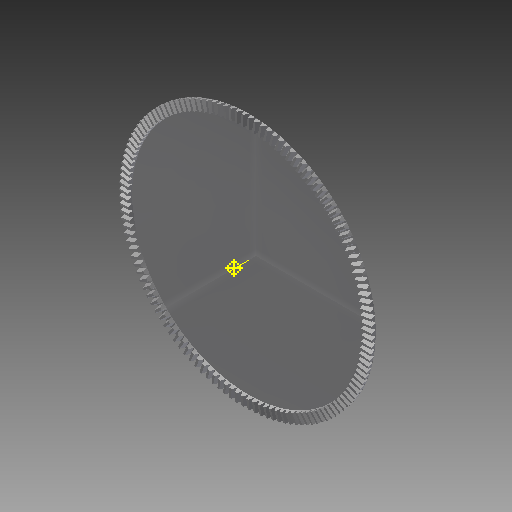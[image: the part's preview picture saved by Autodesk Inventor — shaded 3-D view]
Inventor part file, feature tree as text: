
AUTODESK INVENTOR PART (.ipt)
format: ipt  version: 2017 (Build 210142000, 142)  size: 1,862,656 bytes
history: native  units: mm
features: other x24, loft x2, pattern_circular x2, sketch x1
ambient origin geometry x6: Origin, XZ Plane, X Axis, Y Axis, Z Axis, Center Point
bodies: Solid1 (feature_tree)
feature tree (29):
  other  "Top Point"
  other  "Mesh Plane2"
  other  "Teeth Body"
  other  "Start Point"
  other  "Tooth Plane"
  other  "Start Sketch"
  other  "End Point"
  other  "3D Sketch Right"
  other  "End Plane Right"
  loft  "Loft Right"
  pattern_circular  "Circular Pattern Right"  [2 undecoded]
  other  "3D Sketch Left"
  other  "End Plane Left"
  loft  "Loft Left"
  pattern_circular  "Circular Pattern Left"  [2 undecoded]
  other  "Fix Body"
  other  "Mesh Plane"
  other  "Top Plane"
  other  "Teeth Body Sketch"
  other  "End Plane"
  other  "End Sketch"
  other  "Helical Curve Left"
  other  "End Sketch Left"
  other  "Body Sketch"
  sketch  "Sketch6"  dims[d0=330.2mm d1=329.501251mm d2=330.78229mm d3=12.7mm d4=16.526741mm d5=90.0deg d7=493.522657mm d8=468.312989mm d9=1278.766519mm d11=12.9794mm d12=455.473429mm d15=432.207357mm d16=1180.177168mm d17=0.0mm d18=90.0deg d19=0.0mm d20=90.0deg d21=1300.0mm d22=360.0deg d26=314.208686mm d27=1.487752mm d28=330.2mm d29=-14.559197mm d30=455.473429mm d31=432.207357mm d32=1180.177168mm d35=0.0mm d37=0.0mm d39=0.0mm d40=90.0deg d41=1300.0mm d42=360.0deg d46=90.0deg d47=90.0deg d48=0.0mm d49=0.0mm d50=90.0deg d51=0.241661mm d52=0.0mm d53=0.0mm d54=0.0mm d56=17.557566mm d57=1444.576572mm d58=1436.641612mm d59=1333.203726mm d60=1325.880529mm d61=1333.203726mm d62=1325.880529mm d63=90.0deg d64=90.0deg d65=314.208686mm d66=31.5mm d67=330.2mm d68=-14.559197mm d69=1.487752mm d70=432.207357mm d71=1180.177168mm d72=455.473429mm d73=1325.880529mm d74=1333.203726mm d75=0.0mm d76=90.0deg d77=0.0mm d78=90.0deg d79=0.0mm d80=90.0deg d81=1300.0mm d82=360.0deg d84=10.0mm d85=20.0mm d86=20.0mm d87=10.0mm d88=0.0mm d89=0.0mm]
  other  "Srf1"
  other  "Helical Curve Right"
  other  "End Sketch Right"
  other  "Pitch Diameter"
note: 4 required parameter values undecoded (feature->parameter linkage not recoverable at this tier; creation-order binding heuristic only, values carry confidence <= 0.55)
